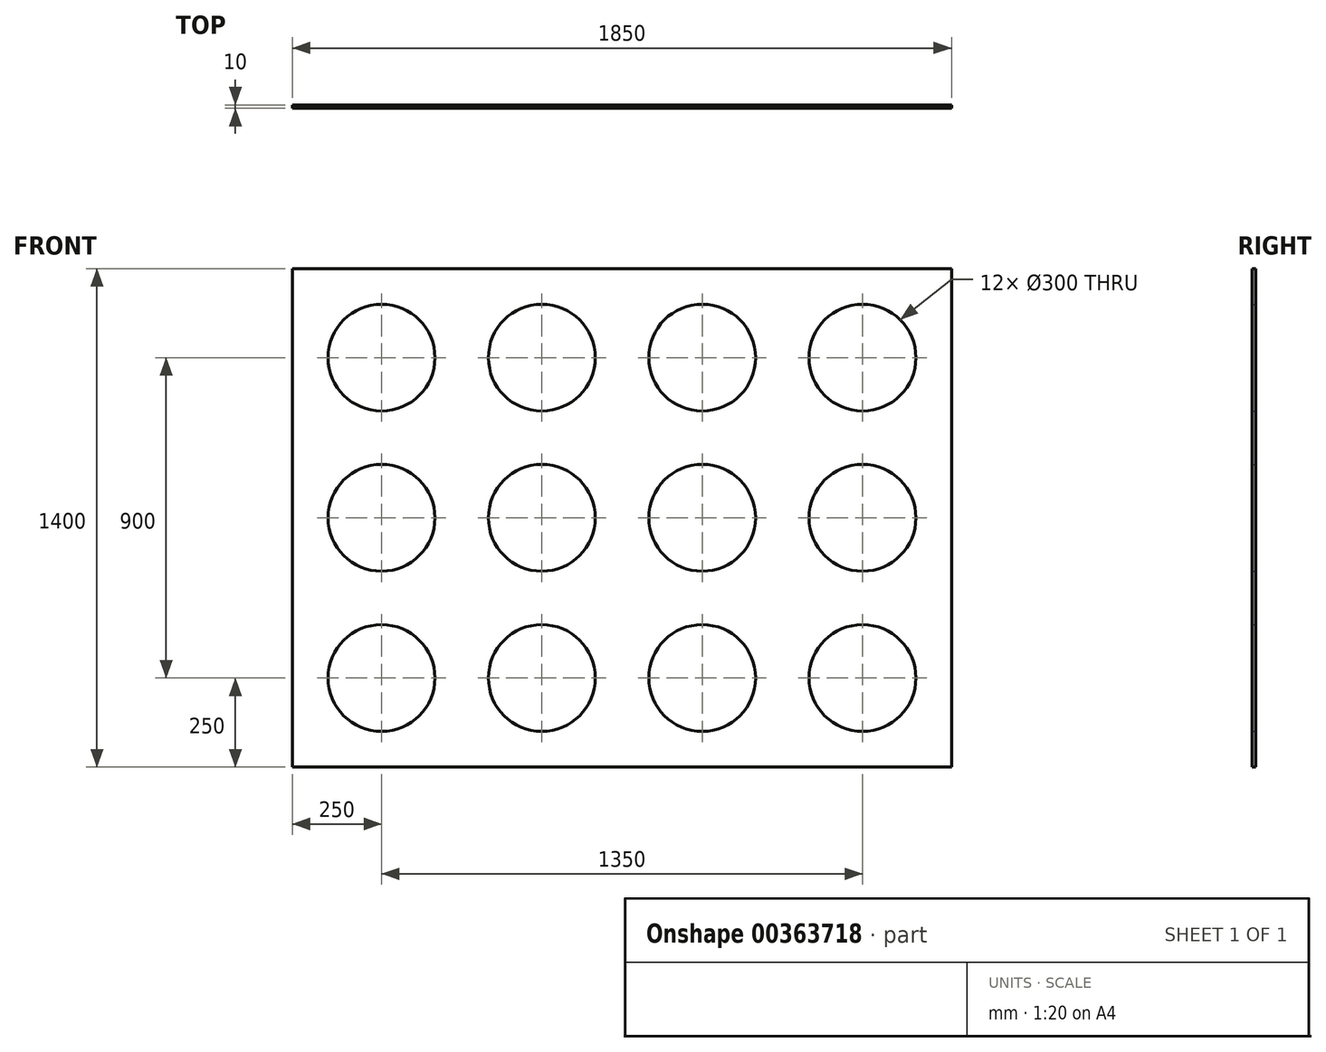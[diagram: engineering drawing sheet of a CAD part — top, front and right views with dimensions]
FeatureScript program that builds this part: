
annotation { "Feature Type Name" : "Feature", "Feature Type Description" : "" }
export const myFeature = defineFeature(function(context is Context, id is Id, definition is map)
    precondition{}
    {
        {
            var Q0;
            Q0=qCreatedBy(makeId("Front.planeOp"),FACE);
            var sketch = newSketch(context, id + "F0", { "sketchPlane" : qUnion([Q0])});
            skLineSegment(sketch, "E0.bottom", {"start": v(925, 700) * mm, "end": v(-925, 700) * mm});
            skLineSegment(sketch, "E0.top", {"start": v(925, -700) * mm, "end": v(-925, -700) * mm});
            skLineSegment(sketch, "E0.left", {"start": v(925, 700) * mm, "end": v(925, -700) * mm});
            skLineSegment(sketch, "E0.right", {"start": v(-925, 700) * mm, "end": v(-925, -700) * mm});
            skPoint(sketch, "E0.middle", {"position": v(0, 0) * mm});
            skCircle(sketch, "E1", {"center": v(-675, -450) * mm, "radius": 150 * mm});
            skCircle(sketch, "E2", {"center": v(-675, 0) * mm, "radius": 150 * mm});
            skCircle(sketch, "E3", {"center": v(-675, 450) * mm, "radius": 150 * mm});
            skCircle(sketch, "E4.MirrorC", {"center": v(-225, 450) * mm, "radius": 150 * mm});
            skCircle(sketch, "E5.MirrorC", {"center": v(-225, 0) * mm, "radius": 150 * mm});
            skCircle(sketch, "E6.MirrorC", {"center": v(-225, -450) * mm, "radius": 150 * mm});
            skCircle(sketch, "E7.MirrorC", {"center": v(225, 450) * mm, "radius": 150 * mm});
            skCircle(sketch, "E8.MirrorC", {"center": v(225, 0) * mm, "radius": 150 * mm});
            skCircle(sketch, "E9.MirrorC", {"center": v(225, -450) * mm, "radius": 150 * mm});
            skCircle(sketch, "E10.MirrorC", {"center": v(675, 450) * mm, "radius": 150 * mm});
            skCircle(sketch, "E11.MirrorC", {"center": v(675, 0) * mm, "radius": 150 * mm});
            skCircle(sketch, "E12.MirrorC", {"center": v(675, -450) * mm, "radius": 150 * mm});
            skSolve(sketch);
        }
        {
            var Q0;
            Q0=makeQuery(id+"F0.imprint","IMPRINT",FACE,{"disambiguationData":[TD([[makeQuery(id+"F0.imprint","IMPRINT",EDGE,{"derivedFrom":sQuery(id+"F0.wireOp",EDGE,"E0.bottom")}),1.0]])]});
            extrude(context, id + "F1", {"entities" : qUnion([Q0]), "depth" : 10 * mm});
        }
    });
